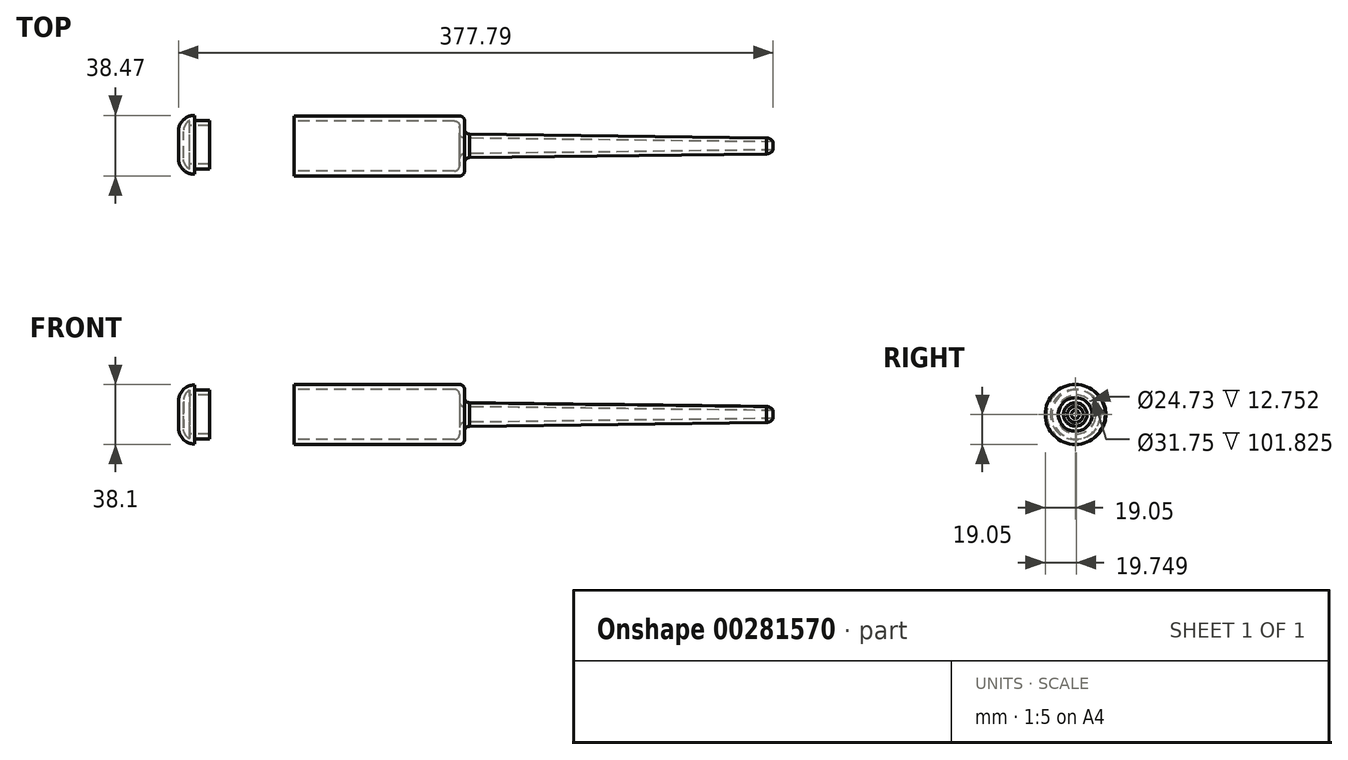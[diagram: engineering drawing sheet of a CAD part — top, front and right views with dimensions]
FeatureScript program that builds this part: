
annotation { "Feature Type Name" : "Feature", "Feature Type Description" : "" }
export const myFeature = defineFeature(function(context is Context, id is Id, definition is map)
    precondition{}
    {
        {
            var Q0;
            Q0=qCreatedBy(makeId("Top.planeOp"),FACE);
            var sketch = newSketch(context, id + "F0", { "sketchPlane" : qUnion([Q0])});
            skPoint(sketch, "E0", {"position": v(0, 15.87) * mm});
            skLineSegment(sketch, "E1", {"start": v(0, 0) * mm, "end": v(304.8, 0) * mm});
            skLineSegment(sketch, "E2", {"start": v(304.2, 2.5) * mm, "end": v(108.14, 4.96) * mm});
            skLineSegment(sketch, "E3", {"start": v(105, 8.14) * mm, "end": v(105, 12.7) * mm});
            skLineSegment(sketch, "E4", {"start": v(101.83, 15.88) * mm, "end": v(0, 15.87) * mm});
            skPoint(sketch, "E5", {"position": v(0, 19.05) * mm});
            skLineSegment(sketch, "E6", {"start": v(0, 15.87) * mm, "end": v(0, 19.05) * mm});
            skLineSegment(sketch, "E7", {"start": v(0, 19.05) * mm, "end": v(105, 19.05) * mm});
            skLineSegment(sketch, "E8", {"start": v(108.17, 15.88) * mm, "end": v(108.17, 10.6) * mm});
            skLineSegment(sketch, "E9", {"start": v(111.27, 7.46) * mm, "end": v(299.93, 5.06) * mm});
            skPoint(sketch, "E10", {"position": v(101.83, 12.7) * mm});
            skArc(sketch, "E11", {"start": v(101.83, 15.88) * mm, "mid": v(104.07, 14.95) * mm, "end": v(105, 12.7) * mm});
            skArc(sketch, "E12", {"start": v(105, 19.05) * mm, "mid": v(107.25, 18.12) * mm, "end": v(108.18, 15.88) * mm});
            skPoint(sketch, "E13.orphan", {"position": v(108.17, 19.05) * mm});
            skPoint(sketch, "E14", {"position": v(111.35, 10.63) * mm});
            skArc(sketch, "E15", {"start": v(111.35, 7.46) * mm, "mid": v(109.1, 8.4) * mm, "end": v(108.17, 10.68) * mm});
            skPoint(sketch, "E16.orphan", {"position": v(108.17, 7.5) * mm});
            skPoint(sketch, "E17", {"position": v(108.17, 8.14) * mm});
            skArc(sketch, "E18", {"start": v(105, 8.14) * mm, "mid": v(105.92, 5.9) * mm, "end": v(108.14, 4.96) * mm});
            skPoint(sketch, "E19", {"position": v(299.8, 0) * mm});
            skArc(sketch, "E20", {"start": v(299.8, 5.06) * mm, "mid": v(302.34, 4.38) * mm, "end": v(304.2, 2.5) * mm});
            skPoint(sketch, "E21.orphan", {"position": v(304.8, 2.5) * mm});
            skPoint(sketch, "E22.orphan", {"position": v(304.8, 5) * mm});
            skSolve(sketch);
        }
        {
            var Q0;
            {var subQ9=sQuery(id+"F0.wireOp",EDGE,"E2");Q0=makeQuery(id+"F0.imprint","IMPRINT",FACE,{"disambiguationData":[TD([[makeQuery(id+"F0.imprint","IMPRINT",EDGE,{"derivedFrom":subQ9}),-1.0]])]});}
            var Q1;
            Q1=sQuery(id+"F0.wireOp",EDGE,"E1");
            revolve(context, id + "F1", {"entities" : qUnion([Q0]), "axis" : qUnion([Q1]), "revolveType" : RevolveType.FULL});
        }
        {
            var Q0;
            Q0=qCreatedBy(makeId("Top.planeOp"),FACE);
            var sketch = newSketch(context, id + "F2", { "sketchPlane" : qUnion([Q0])});
            skLineSegment(sketch, "E23", {"start": v(-53.72, 16.24) * mm, "end": v(-63.3, 16.24) * mm});
            skLineSegment(sketch, "E24", {"start": v(-63.3, 16.24) * mm, "end": v(-63.3, 19.42) * mm});
            skLineSegment(sketch, "E25", {"start": v(-73.6, 9.12) * mm, "end": v(-73.6, 0.7) * mm});
            skPoint(sketch, "E26", {"position": v(-73.6, 9.12) * mm});
            skArc(sketch, "E27", {"start": v(-73.6, 9.12) * mm, "mid": v(-70.58, 16.4) * mm, "end": v(-63.3, 19.42) * mm});
            skPoint(sketch, "E28.end.orphan", {"position": v(-73.6, 19.75) * mm});
            skLineSegment(sketch, "E29", {"start": v(-73.6, 0.7) * mm, "end": v(-70.42, 0.7) * mm});
            skLineSegment(sketch, "E30", {"start": v(-70.42, 0.7) * mm, "end": v(-70.42, 9.12) * mm});
            skPoint(sketch, "E31.endSnap0", {"position": v(-63.3, 16.24) * mm});
            skLineSegment(sketch, "E32", {"start": v(-66.47, 16.24) * mm, "end": v(-66.47, 13.07) * mm});
            skLineSegment(sketch, "E33", {"start": v(-66.47, 13.07) * mm, "end": v(-53.72, 13.07) * mm});
            skLineSegment(sketch, "E34", {"start": v(-53.72, 13.07) * mm, "end": v(-53.72, 16.24) * mm});
            skArc(sketch, "E35", {"start": v(-66.47, 16.24) * mm, "mid": v(-69.36, 13.2) * mm, "end": v(-70.42, 9.12) * mm});
            skSolve(sketch);
        }
        {
            var Q0;
            Q0=makeQuery(id+"F2.imprint","IMPRINT",FACE,{"disambiguationData":[TD([[makeQuery(id+"F2.imprint","IMPRINT",EDGE,{"derivedFrom":sQuery(id+"F2.wireOp",EDGE,"E23")}),1.0]])]});
            var Q1;
            Q1=sQuery(id+"F2.wireOp",EDGE,"E29");
            revolve(context, id + "F3", {"entities" : qUnion([Q0]), "axis" : qUnion([Q1]), "revolveType" : RevolveType.FULL});
        }
    });
